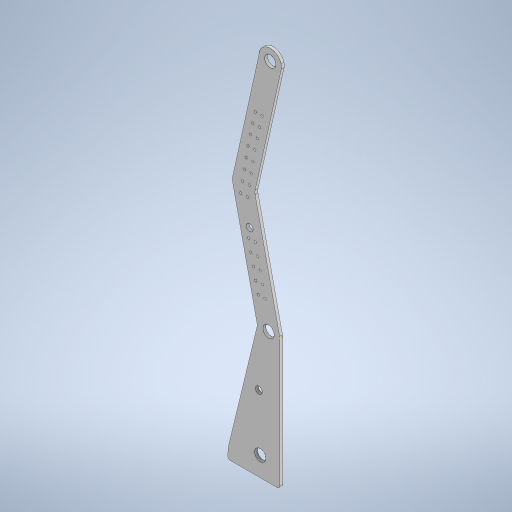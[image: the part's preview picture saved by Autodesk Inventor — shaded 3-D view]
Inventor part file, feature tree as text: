
AUTODESK INVENTOR PART (.ipt)
format: ipt  version: 2023 (Build 270158000, 158)  size: 555,008 bytes
history: native  units: in
note: dims shown in document units (in); Inventor stores cm internally (conversion verified against a paired STEP export)
features: sketch x18, extrude x16, fillet x2, projected_geometry x1
ambient origin geometry x8: Origin, YZ Plane, XZ Plane, XY Plane, X Axis, Y Axis, Z Axis, Center Point
bodies: Body1 (feature_tree), Body2 (feature_tree), Body3 (feature_tree)
feature tree (37):
  extrude  "Extrusion3"  Depth=0.7043in
  sketch  "Sketch3"  dims[d0=4.5in d1=0.7043in]
  extrude  "Extrusion14"  Depth=1.0651in
  extrude  "Extrusion15"  Depth=1.0in
  extrude  "Extrusion16"  Depth=0.5in
  extrude  "Extrusion17"  Depth=0.5in
  extrude  "Extrusion18"  Depth=0.5in
  extrude  "Extrusion19"  Depth=1.0in
  extrude  "Extrusion20"  Depth=0.5in
  sketch  "Sketch11"  dims[d25=0.5325in d26=1.0in]
  sketch  "Sketch12"  dims[d27=1.0in d28=0.5in d29=0.5in]
  fillet  "Fillet1"  Radius=0.5in
  sketch  "Sketch13"  dims[d30=0.25in d31=0.0in d42=1.0in]
  sketch  "Sketch33"  dims[d50=1.5in d51=0.25in]
  extrude  "Extrusion43"  Depth=1.0in
  extrude  "Extrusion44"  Depth=0.25in
  extrude  "Extrusion45"  Depth=0.585in
  extrude  "Extrusion46"  Depth=1.0in TaperAngle=0.0deg
  sketch  "Sketch41"  dims[d91=0.5in d92=0.5in d93=0.5in]
  extrude  "Extrusion48"  Depth=1.0in TaperAngle=0.0deg
  extrude  "Extrusion49"  Depth=1.0in
  extrude  "Extrusion50"  Depth=0.5in
  fillet  "Fillet2"  Radius=0.5in
  extrude  "Extrusion51"  Depth=0.5in
  sketch  "Sketch6"  dims[d2=4.5in d3=1.0651in]
  sketch  "Sketch7"  dims[d4=1.0in d5=1.0in]
  sketch  "Sketch8"  dims[d6=1.0in d7=0.5in]
  projected_geometry  "Projected Loop1"
  sketch  "Sketch9"  dims[d8=0.5in d9=0.5in]
  sketch  "Sketch10"  dims[d10=0.5in d24=5.5in]
  sketch  "Sketch37"  dims[d59=0.3in d76=0.585in]
  sketch  "Sketch38"  dims[d77=0.585in d78=1.0in d79=0.0in]
  sketch  "Sketch39"  dims[d82=0.1in d83=1.0in d84=0.0in]
  sketch  "Sketch40"  dims[d89=1.0in d90=0.5325in]
  sketch  "Sketch42"  dims[d94=0.5in d95=0.1in]
  sketch  "Sketch43"  dims[d96=0.1in]
  sketch  "Sketch44"  dims[d97=0.1in d98=0.1in d99=0.1in d100=1.0in d101=0.0in d102=0.6in d103=0.1in d104=1.0in d105=0.0in d106=0.125in d107=0.0in d108=2.0in d109=0.3in d110=0.3in d111=0.3in d112=0.3in d113=0.3in d114=0.3in d115=0.3in d116=0.1in d117=0.1in d118=0.1in d119=0.1in d120=0.1in d121=0.1in d122=0.1in d123=0.5in d124=0.5in d125=0.5in d126=0.5in d127=0.5325in d128=0.5in d129=0.5in d130=0.3in d131=0.3in d132=0.3in d133=0.3in d134=0.3in d135=0.3in d136=0.3in d137=0.1in d138=0.1in d139=0.1in d140=0.1in d141=0.1in d142=0.1in d143=0.1in d144=0.1in d145=0.1in d146=0.1in d147=0.1in d148=0.1in d149=0.1in d150=0.1in d151=0.125in d152=0.0in d153=0.125in d154=0.0in d155=0.4in d240=6.0in d241=1.0in d242=0.125in d243=0.0in d244=0.125in d245=0.0in d246=0.2in d247=0.5in d248=0.125in d249=0.0in d250=0.5in d251=0.125in d252=0.0in d253=0.5in d257=0.5in d258=0.125in d259=0.0in d260=2.5in d261=0.6871in d262=0.3in d263=0.125in d264=0.0in d265=0.3in d266=0.1718in d267=0.585in d268=0.5in d269=0.5in d270=0.5in d271=0.125in d272=0.0in d273=0.125in d274=1.0in d275=0.0in d60=0.0344in d61=0.5in d62=0.0344in d74=0.5in d75=0.0344in d80=0.5in d81=0.0344in d158=0.5in d159=0.0344in d160=0.5in d161=0.0344in d162=0.5in d163=0.0344in d164=0.5in d165=0.0344in d202=0.5in d203=0.0344in d204=0.5in d205=0.0344in d229=0.5in d230=0.0344in d231=0.5in d232=0.0344in]
